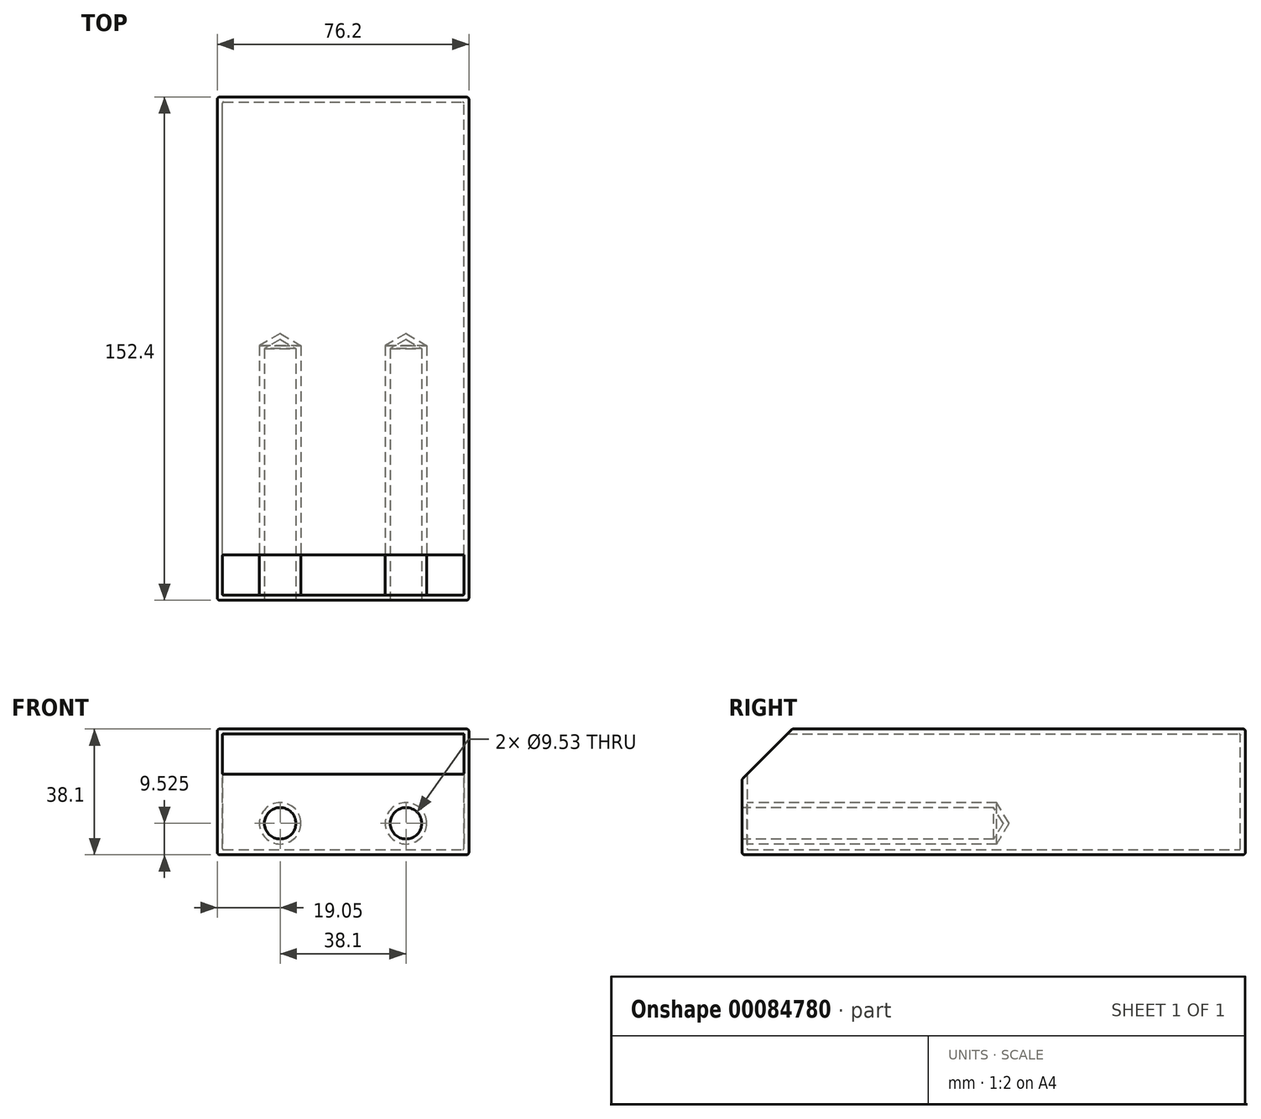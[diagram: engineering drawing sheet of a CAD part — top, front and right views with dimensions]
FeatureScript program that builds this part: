
annotation { "Feature Type Name" : "Feature", "Feature Type Description" : "" }
export const myFeature = defineFeature(function(context is Context, id is Id, definition is map)
    precondition{}
    {
        {
            assignVariable(context, id + "F0", {"name" : "l", "anyValue" : 76.2 * mm});
        }
        {
            assignVariable(context, id + "F1", {"name" : "d", "anyValue" : getVariable(context, 'l') * 2});
        }
        {
            var Q0;
            Q0=qCreatedBy(makeId("Front.planeOp"),FACE);
            var sketch = newSketch(context, id + "F2", { "sketchPlane" : qUnion([Q0])});
            skLineSegment(sketch, "E0.bottom", {"start": v(0, 0) * mm, "end": v(76.2, 0) * mm});
            skLineSegment(sketch, "E0.top", {"start": v(0, 38.1) * mm, "end": v(76.2, 38.1) * mm});
            skLineSegment(sketch, "E0.left", {"start": v(0, 0) * mm, "end": v(0, 38.1) * mm});
            skLineSegment(sketch, "E0.right", {"start": v(76.2, 0) * mm, "end": v(76.2, 38.1) * mm});
            skSolve(sketch);
        }
        {
            var Q0;
            Q0 = qSketchRegion(id + "F2", true);
            extrude(context, id + "F3", {"entities" : qUnion([Q0]), "oppositeDirection" : true, "depth" : getVariable(context, 'd')});
        }
        {
            var Q0;
            Q0=qCreatedBy(makeId("Front.planeOp"),FACE);
            var sketch = newSketch(context, id + "F4", { "sketchPlane" : qUnion([Q0])});
            skPoint(sketch, "E1", {"position": v(19.05, 9.53) * mm});
            skPoint(sketch, "E2", {"position": v(57.15, 9.53) * mm});
            skSolve(sketch);
        }
        {
            var Q0;
            Q0=sQuery(id+"F4.wireOp",VERTEX,"E2");
            var Q1;
            Q1=sQuery(id+"F4.wireOp",VERTEX,"E1");
            var Q2;
            Q2=makeQuery(id+"F3.opExtrude","SWEPT_BODY",BODY,{"disambiguationData":[OSD([sQuery(id+"F2.wireOp",EDGE,"E0.bottom"),sQuery(id+"F2.wireOp",EDGE,"E0.top"),sQuery(id+"F2.wireOp",EDGE,"E0.left"),sQuery(id+"F2.wireOp",EDGE,"E0.right")])]});
            hole(context, id + "F5", {"style" : HoleStyle.SIMPLE, "endStyle" : HoleEndStyle.BLIND, "holeDiameter" : getVariable(context, 'l') / 8, "holeDepth" : getVariable(context, 'd') / 2, "startFromSketch" : true, "locations" : qUnion([Q0, Q1]), "scope" : qUnion([Q2])});
        }
        {
            var Q0;
            Q0=makeQuery(id+"F3.opExtrude","CAP_EDGE",EDGE,{"disambiguationData":[OSD([sQuery(id+"F2.wireOp",EDGE,"E0.top")])],"isStart":true});
            chamfer(context, id + "F6", {"entities" : qUnion([Q0]), "width" : getVariable(context, 'l') / 5, "tangentPropagation" : true});
        }
        {
            var Q0;
            Q0=makeQuery(id+"F3.opExtrude","SWEPT_EDGE",EDGE,{"disambiguationData":[OSD([sQuery(id+"F2.wireOp",EDGE,"E0.top"),sQuery(id+"F2.wireOp",EDGE,"E0.right")])]});
            var Q1;
            Q1=makeQuery(id+"F3.opExtrude","SWEPT_EDGE",EDGE,{"disambiguationData":[OSD([sQuery(id+"F2.wireOp",EDGE,"E0.top"),sQuery(id+"F2.wireOp",EDGE,"E0.left")])]});
            var Q2;
            Q2=makeQuery(id+"F3.opExtrude","SWEPT_EDGE",EDGE,{"disambiguationData":[OSD([sQuery(id+"F2.wireOp",EDGE,"E0.bottom"),sQuery(id+"F2.wireOp",EDGE,"E0.left")])]});
            var Q3;
            Q3=makeQuery(id+"F3.opExtrude","SWEPT_EDGE",EDGE,{"disambiguationData":[OSD([sQuery(id+"F2.wireOp",EDGE,"E0.bottom"),sQuery(id+"F2.wireOp",EDGE,"E0.right")])]});
            var Q4;
            {var subQ0=sQuery(id+"F2.wireOp",EDGE,"E0.top");Q4=makeQuery(id+"F6.opChamfer","BLEND_EDGE",EDGE,{"blendedFrom":[makeQuery(id+"F3.opExtrude","CAP_EDGE",EDGE,{"disambiguationData":[OSD([subQ0])],"isStart":true}),makeQuery(id+"F3.opExtrude","SWEPT_FACE",FACE,{"disambiguationData":[OSD([subQ0])]})],"blendedInto":[makeQuery(id+"F3.opExtrude","SWEPT_FACE",FACE,{"disambiguationData":[OSD([subQ0])]})]});}
            var Q5;
            {var subQ0=sQuery(id+"F2.wireOp",EDGE,"E0.top");Q5=makeQuery(id+"F6.opChamfer","BLEND_EDGE",EDGE,{"blendedFrom":[makeQuery(id+"F3.opExtrude","CAP_EDGE",EDGE,{"disambiguationData":[OSD([subQ0])],"isStart":true}),makeQuery(id+"F3.opExtrude","CAP_FACE",FACE,{"disambiguationData":[OSD([sQuery(id+"F2.wireOp",EDGE,"E0.bottom"),subQ0,sQuery(id+"F2.wireOp",EDGE,"E0.left"),sQuery(id+"F2.wireOp",EDGE,"E0.right")])],"isStart":true})],"blendedInto":[makeQuery(id+"F3.opExtrude","CAP_FACE",FACE,{"disambiguationData":[OSD([sQuery(id+"F2.wireOp",EDGE,"E0.bottom"),subQ0,sQuery(id+"F2.wireOp",EDGE,"E0.left"),sQuery(id+"F2.wireOp",EDGE,"E0.right")])],"isStart":true})]});}
            var Q6;
            Q6=makeQuery(id+"F3.opExtrude","CAP_EDGE",EDGE,{"disambiguationData":[OSD([sQuery(id+"F2.wireOp",EDGE,"E0.bottom")])],"isStart":true});
            var Q7;
            Q7=makeQuery(id+"F6.opChamfer","BLEND_EDGE",EDGE,{"blendedFrom":[makeQuery(id+"F3.opExtrude","CAP_EDGE",EDGE,{"disambiguationData":[OSD([sQuery(id+"F2.wireOp",EDGE,"E0.top")])],"isStart":true}),makeQuery(id+"F3.opExtrude","SWEPT_FACE",FACE,{"disambiguationData":[OSD([sQuery(id+"F2.wireOp",EDGE,"E0.right")])]})],"blendedInto":[makeQuery(id+"F3.opExtrude","SWEPT_FACE",FACE,{"disambiguationData":[OSD([sQuery(id+"F2.wireOp",EDGE,"E0.right")])]})]});
            var Q8;
            Q8=makeQuery(id+"F6.opChamfer","BLEND_EDGE",EDGE,{"blendedFrom":[makeQuery(id+"F3.opExtrude","CAP_EDGE",EDGE,{"disambiguationData":[OSD([sQuery(id+"F2.wireOp",EDGE,"E0.top")])],"isStart":true}),makeQuery(id+"F3.opExtrude","SWEPT_FACE",FACE,{"disambiguationData":[OSD([sQuery(id+"F2.wireOp",EDGE,"E0.left")])]})],"blendedInto":[makeQuery(id+"F3.opExtrude","SWEPT_FACE",FACE,{"disambiguationData":[OSD([sQuery(id+"F2.wireOp",EDGE,"E0.left")])]})]});
            var Q9;
            Q9=makeQuery(id+"F3.opExtrude","CAP_EDGE",EDGE,{"disambiguationData":[OSD([sQuery(id+"F2.wireOp",EDGE,"E0.top")])],"isStart":false});
            var Q10;
            Q10=makeQuery(id+"F3.opExtrude","CAP_EDGE",EDGE,{"disambiguationData":[OSD([sQuery(id+"F2.wireOp",EDGE,"E0.right")])],"isStart":false});
            var Q11;
            Q11=makeQuery(id+"F3.opExtrude","CAP_EDGE",EDGE,{"disambiguationData":[OSD([sQuery(id+"F2.wireOp",EDGE,"E0.left")])],"isStart":false});
            var Q12;
            Q12=makeQuery(id+"F3.opExtrude","CAP_EDGE",EDGE,{"disambiguationData":[OSD([sQuery(id+"F2.wireOp",EDGE,"E0.bottom")])],"isStart":false});
            var Q13;
            Q13=makeQuery(id+"F3.opExtrude","CAP_EDGE",EDGE,{"disambiguationData":[OSD([sQuery(id+"F2.wireOp",EDGE,"E0.right")])],"isStart":true});
            var Q14;
            Q14=makeQuery(id+"F3.opExtrude","CAP_EDGE",EDGE,{"disambiguationData":[OSD([sQuery(id+"F2.wireOp",EDGE,"E0.left")])],"isStart":true});
            fillet(context, id + "F7", {"entities" : qUnion([Q0, Q1, Q2, Q3, Q4, Q5, Q6, Q7, Q8, Q9, Q10, Q11, Q12, Q13, Q14]), "radius" : getVariable(context, 'l') / 100, "tangentPropagation" : true, "allowEdgeOverflow" : false});
        }
        {
            var Q0;
            Q0=makeQuery(id+"F6.opChamfer","BLEND_FACE",FACE,{"disambiguationData":[OSD([sQuery(id+"F2.wireOp",EDGE,"E0.top")])]});
            shell(context, id + "F8", {"entities" : qUnion([Q0]), "thickness" : getVariable(context, 'l') / 50});
        }
        {
            var Q0;
            Q0=makeQuery(id+"F8.opShell","OFFSET_EDGE",EDGE,{"disambiguationData":[OSD([sQuery(id+"F2.wireOp",EDGE,"E0.bottom"),sQuery(id+"F2.wireOp",EDGE,"E0.right")])]});
            var Q1;
            {var subQ0=sQuery(id+"F2.wireOp",EDGE,"E0.right");var subQ1=makeQuery(id+"F3.opExtrude","CAP_EDGE",EDGE,{"disambiguationData":[OSD([subQ0])],"isStart":false});var subQ2=sQuery(id+"F2.wireOp",EDGE,"E0.left");var subQ3=sQuery(id+"F2.wireOp",EDGE,"E0.top");var subQ4=sQuery(id+"F2.wireOp",EDGE,"E0.bottom");Q1=makeQuery(id+"F8.opShell","OFFSET_EDGE",EDGE,{"disambiguationData":[OSD([subQ4,subQ3,subQ2,subQ0]),TDD([makeQuery(id+"F7.opFillet","BLEND_EDGE",EDGE,{"blendedFrom":[subQ1,makeQuery(id+"F3.opExtrude","CAP_FACE",FACE,{"disambiguationData":[OSD([subQ4,subQ3,subQ2,subQ0])],"isStart":false})],"blendedInto":[makeQuery(id+"F3.opExtrude","CAP_FACE",FACE,{"disambiguationData":[OSD([subQ4,subQ3,subQ2,subQ0])],"isStart":false})]}),makeQuery(id+"F7.opFillet","BLEND_EDGE",EDGE,{"blendedFrom":[subQ1,makeQuery(id+"F3.opExtrude","SWEPT_FACE",FACE,{"disambiguationData":[OSD([subQ0])]})],"blendedInto":[makeQuery(id+"F3.opExtrude","SWEPT_FACE",FACE,{"disambiguationData":[OSD([subQ0])]})]})])]});}
            var Q2;
            {var subQ0=sQuery(id+"F2.wireOp",EDGE,"E0.right");var subQ1=sQuery(id+"F2.wireOp",EDGE,"E0.left");var subQ2=sQuery(id+"F2.wireOp",EDGE,"E0.top");var subQ3=sQuery(id+"F2.wireOp",EDGE,"E0.bottom");var subQ4=makeQuery(id+"F3.opExtrude","CAP_EDGE",EDGE,{"disambiguationData":[OSD([subQ3])],"isStart":false});Q2=makeQuery(id+"F8.opShell","OFFSET_EDGE",EDGE,{"disambiguationData":[OSD([subQ3,subQ2,subQ1,subQ0]),TDD([makeQuery(id+"F7.opFillet","BLEND_EDGE",EDGE,{"blendedFrom":[subQ4,makeQuery(id+"F3.opExtrude","SWEPT_FACE",FACE,{"disambiguationData":[OSD([subQ3])]})],"blendedInto":[makeQuery(id+"F3.opExtrude","SWEPT_FACE",FACE,{"disambiguationData":[OSD([subQ3])]})]}),makeQuery(id+"F7.opFillet","BLEND_EDGE",EDGE,{"blendedFrom":[subQ4,makeQuery(id+"F3.opExtrude","CAP_FACE",FACE,{"disambiguationData":[OSD([subQ3,subQ2,subQ1,subQ0])],"isStart":false})],"blendedInto":[makeQuery(id+"F3.opExtrude","CAP_FACE",FACE,{"disambiguationData":[OSD([subQ3,subQ2,subQ1,subQ0])],"isStart":false})]})])]});}
            var Q3;
            {var subQ0=sQuery(id+"F2.wireOp",EDGE,"E0.top");var subQ1=makeQuery(id+"F3.opExtrude","CAP_EDGE",EDGE,{"disambiguationData":[OSD([subQ0])],"isStart":false});var subQ2=sQuery(id+"F2.wireOp",EDGE,"E0.right");var subQ3=sQuery(id+"F2.wireOp",EDGE,"E0.left");var subQ4=sQuery(id+"F2.wireOp",EDGE,"E0.bottom");Q3=makeQuery(id+"F8.opShell","OFFSET_EDGE",EDGE,{"disambiguationData":[OSD([subQ4,subQ0,subQ3,subQ2]),TDD([makeQuery(id+"F7.opFillet","BLEND_EDGE",EDGE,{"blendedFrom":[subQ1,makeQuery(id+"F3.opExtrude","CAP_FACE",FACE,{"disambiguationData":[OSD([subQ4,subQ0,subQ3,subQ2])],"isStart":false})],"blendedInto":[makeQuery(id+"F3.opExtrude","CAP_FACE",FACE,{"disambiguationData":[OSD([subQ4,subQ0,subQ3,subQ2])],"isStart":false})]}),makeQuery(id+"F7.opFillet","BLEND_EDGE",EDGE,{"blendedFrom":[subQ1,makeQuery(id+"F3.opExtrude","SWEPT_FACE",FACE,{"disambiguationData":[OSD([subQ0])]})],"blendedInto":[makeQuery(id+"F3.opExtrude","SWEPT_FACE",FACE,{"disambiguationData":[OSD([subQ0])]})]})])]});}
            var Q4;
            {var subQ0=sQuery(id+"F2.wireOp",EDGE,"E0.left");var subQ1=makeQuery(id+"F3.opExtrude","CAP_EDGE",EDGE,{"disambiguationData":[OSD([subQ0])],"isStart":false});var subQ2=sQuery(id+"F2.wireOp",EDGE,"E0.right");var subQ3=sQuery(id+"F2.wireOp",EDGE,"E0.top");var subQ4=sQuery(id+"F2.wireOp",EDGE,"E0.bottom");Q4=makeQuery(id+"F8.opShell","OFFSET_EDGE",EDGE,{"disambiguationData":[OSD([subQ4,subQ3,subQ0,subQ2]),TDD([makeQuery(id+"F7.opFillet","BLEND_EDGE",EDGE,{"blendedFrom":[subQ1,makeQuery(id+"F3.opExtrude","CAP_FACE",FACE,{"disambiguationData":[OSD([subQ4,subQ3,subQ0,subQ2])],"isStart":false})],"blendedInto":[makeQuery(id+"F3.opExtrude","CAP_FACE",FACE,{"disambiguationData":[OSD([subQ4,subQ3,subQ0,subQ2])],"isStart":false})]}),makeQuery(id+"F7.opFillet","BLEND_EDGE",EDGE,{"blendedFrom":[subQ1,makeQuery(id+"F3.opExtrude","SWEPT_FACE",FACE,{"disambiguationData":[OSD([subQ0])]})],"blendedInto":[makeQuery(id+"F3.opExtrude","SWEPT_FACE",FACE,{"disambiguationData":[OSD([subQ0])]})]})])]});}
            var Q5;
            {var subQ0=sQuery(id+"F2.wireOp",EDGE,"E0.left");var subQ1=sQuery(id+"F2.wireOp",EDGE,"E0.top");var subQ2=makeQuery(id+"F3.opExtrude","SWEPT_EDGE",EDGE,{"disambiguationData":[OSD([subQ1,subQ0])]});Q5=makeQuery(id+"F8.opShell","OFFSET_EDGE",EDGE,{"disambiguationData":[OSD([subQ1,subQ0]),TDD([makeQuery(id+"F7.opFillet","BLEND_EDGE",EDGE,{"blendedFrom":[subQ2,makeQuery(id+"F3.opExtrude","SWEPT_FACE",FACE,{"disambiguationData":[OSD([subQ1])]})],"blendedInto":[makeQuery(id+"F3.opExtrude","SWEPT_FACE",FACE,{"disambiguationData":[OSD([subQ1])]})]}),makeQuery(id+"F7.opFillet","BLEND_EDGE",EDGE,{"blendedFrom":[subQ2,makeQuery(id+"F3.opExtrude","SWEPT_FACE",FACE,{"disambiguationData":[OSD([subQ0])]})],"blendedInto":[makeQuery(id+"F3.opExtrude","SWEPT_FACE",FACE,{"disambiguationData":[OSD([subQ0])]})]})])]});}
            var Q6;
            Q6=makeQuery(id+"F8.opShell","OFFSET_EDGE",EDGE,{"disambiguationData":[OSD([sQuery(id+"F2.wireOp",EDGE,"E0.bottom"),sQuery(id+"F2.wireOp",EDGE,"E0.left")])]});
            var Q7;
            {var subQ0=sQuery(id+"F2.wireOp",EDGE,"E0.right");var subQ1=sQuery(id+"F2.wireOp",EDGE,"E0.left");var subQ2=sQuery(id+"F2.wireOp",EDGE,"E0.top");var subQ3=sQuery(id+"F2.wireOp",EDGE,"E0.bottom");var subQ4=makeQuery(id+"F3.opExtrude","CAP_EDGE",EDGE,{"disambiguationData":[OSD([subQ3])],"isStart":true});Q7=makeQuery(id+"F8.opShell","OFFSET_EDGE",EDGE,{"disambiguationData":[OSD([subQ3,subQ2,subQ1,subQ0]),TDD([makeQuery(id+"F7.opFillet","BLEND_EDGE",EDGE,{"blendedFrom":[subQ4,makeQuery(id+"F3.opExtrude","SWEPT_FACE",FACE,{"disambiguationData":[OSD([subQ3])]})],"blendedInto":[makeQuery(id+"F3.opExtrude","SWEPT_FACE",FACE,{"disambiguationData":[OSD([subQ3])]})]}),makeQuery(id+"F7.opFillet","BLEND_EDGE",EDGE,{"blendedFrom":[subQ4,makeQuery(id+"F3.opExtrude","CAP_FACE",FACE,{"disambiguationData":[OSD([subQ3,subQ2,subQ1,subQ0])],"isStart":true})],"blendedInto":[makeQuery(id+"F3.opExtrude","CAP_FACE",FACE,{"disambiguationData":[OSD([subQ3,subQ2,subQ1,subQ0])],"isStart":true})]})])]});}
            var Q8;
            {var subQ0=sQuery(id+"F2.wireOp",EDGE,"E0.right");var subQ1=sQuery(id+"F2.wireOp",EDGE,"E0.left");var subQ2=sQuery(id+"F2.wireOp",EDGE,"E0.top");var subQ3=sQuery(id+"F2.wireOp",EDGE,"E0.bottom");var subQ4=makeQuery(id+"F3.opExtrude","CAP_EDGE",EDGE,{"disambiguationData":[OSD([subQ1])],"isStart":true});Q8=makeQuery(id+"F8.opShell","OFFSET_EDGE",EDGE,{"disambiguationData":[OSD([subQ3,subQ2,subQ1,subQ0]),TDD([makeQuery(id+"F7.opFillet","BLEND_EDGE",EDGE,{"blendedFrom":[subQ4,makeQuery(id+"F3.opExtrude","SWEPT_FACE",FACE,{"disambiguationData":[OSD([subQ1])]})],"blendedInto":[makeQuery(id+"F3.opExtrude","SWEPT_FACE",FACE,{"disambiguationData":[OSD([subQ1])]})]}),makeQuery(id+"F7.opFillet","BLEND_EDGE",EDGE,{"blendedFrom":[subQ4,makeQuery(id+"F3.opExtrude","CAP_FACE",FACE,{"disambiguationData":[OSD([subQ3,subQ2,subQ1,subQ0])],"isStart":true})],"blendedInto":[makeQuery(id+"F3.opExtrude","CAP_FACE",FACE,{"disambiguationData":[OSD([subQ3,subQ2,subQ1,subQ0])],"isStart":true})]})])]});}
            var Q9;
            {var subQ0=sQuery(id+"F2.wireOp",EDGE,"E0.right");var subQ1=sQuery(id+"F2.wireOp",EDGE,"E0.left");var subQ2=sQuery(id+"F2.wireOp",EDGE,"E0.top");var subQ3=sQuery(id+"F2.wireOp",EDGE,"E0.bottom");var subQ4=makeQuery(id+"F3.opExtrude","CAP_EDGE",EDGE,{"disambiguationData":[OSD([subQ0])],"isStart":true});Q9=makeQuery(id+"F8.opShell","OFFSET_EDGE",EDGE,{"disambiguationData":[OSD([subQ3,subQ2,subQ1,subQ0]),TDD([makeQuery(id+"F7.opFillet","BLEND_EDGE",EDGE,{"blendedFrom":[subQ4,makeQuery(id+"F3.opExtrude","SWEPT_FACE",FACE,{"disambiguationData":[OSD([subQ0])]})],"blendedInto":[makeQuery(id+"F3.opExtrude","SWEPT_FACE",FACE,{"disambiguationData":[OSD([subQ0])]})]}),makeQuery(id+"F7.opFillet","BLEND_EDGE",EDGE,{"blendedFrom":[subQ4,makeQuery(id+"F3.opExtrude","CAP_FACE",FACE,{"disambiguationData":[OSD([subQ3,subQ2,subQ1,subQ0])],"isStart":true})],"blendedInto":[makeQuery(id+"F3.opExtrude","CAP_FACE",FACE,{"disambiguationData":[OSD([subQ3,subQ2,subQ1,subQ0])],"isStart":true})]})])]});}
            var Q10;
            Q10=makeQuery(id+"F8.opShell","OFFSET_EDGE",EDGE,{"disambiguationData":[OSD([sQuery(id+"F5.hole-1.sketch.wireOp",EDGE,"core_line_2"),sQuery(id+"F5.hole-1.sketch.wireOp",EDGE,"core_line_3")])]});
            var Q11;
            Q11=makeQuery(id+"F8.opShell","OFFSET_EDGE",EDGE,{"disambiguationData":[OSD([sQuery(id+"F5.hole-0.sketch.wireOp",EDGE,"core_line_2"),sQuery(id+"F5.hole-0.sketch.wireOp",EDGE,"core_line_3")])]});
            var Q12;
            Q12=makeQuery(id+"F8.opShell","OFFSET_EDGE",EDGE,{"disambiguationData":[OSD([sQuery(id+"F5.hole-1.sketch.wireOp",EDGE,"core_line_1"),sQuery(id+"F5.hole-1.sketch.wireOp",EDGE,"core_line_2")])]});
            var Q13;
            Q13=makeQuery(id+"F8.opShell","OFFSET_EDGE",EDGE,{"disambiguationData":[OSD([sQuery(id+"F5.hole-0.sketch.wireOp",EDGE,"core_line_1"),sQuery(id+"F5.hole-0.sketch.wireOp",EDGE,"core_line_2")])]});
            fillet(context, id + "F9", {"entities" : qUnion([Q0, Q1, Q2, Q3, Q4, Q5, Q6, Q7, Q8, Q9, Q10, Q11, Q12, Q13]), "radius" : getVariable(context, 'l') / 200, "tangentPropagation" : true, "allowEdgeOverflow" : false});
        }
    });
